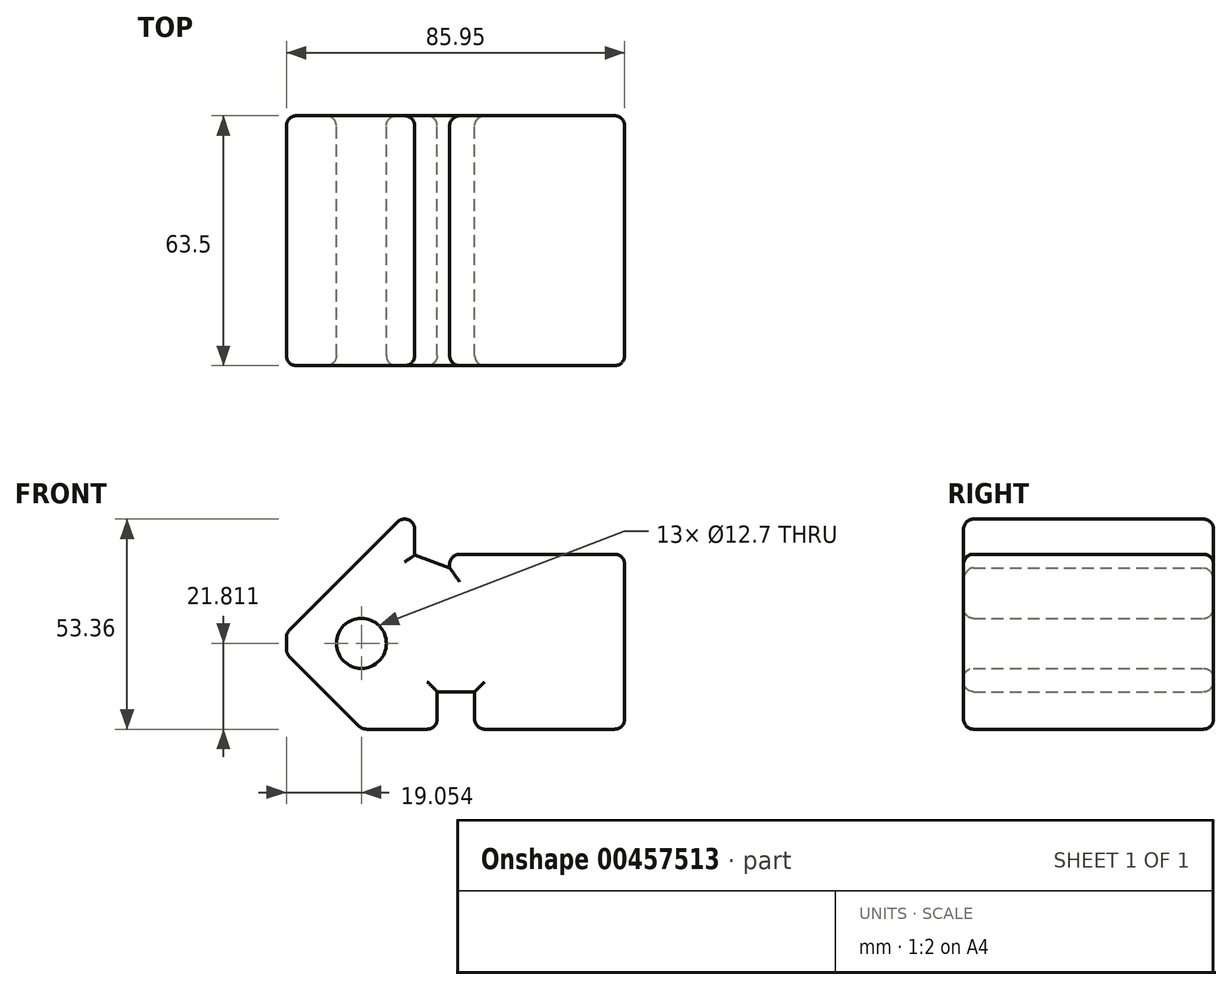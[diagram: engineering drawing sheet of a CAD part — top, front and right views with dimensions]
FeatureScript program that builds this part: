
annotation { "Feature Type Name" : "Feature", "Feature Type Description" : "" }
export const myFeature = defineFeature(function(context is Context, id is Id, definition is map)
    precondition{}
    {
        {
            var Q0;
            Q0=qCreatedBy(makeId("Front.planeOp"),FACE);
            var sketch = newSketch(context, id + "F0", { "sketchPlane" : qUnion([Q0])});
            skLineSegment(sketch, "E0", {"start": v(-44.45, 0) * mm, "end": v(0, 0) * mm});
            skLineSegment(sketch, "E1", {"start": v(0, 0) * mm, "end": v(0, -44.45) * mm});
            skLineSegment(sketch, "E2", {"start": v(0, -44.45) * mm, "end": v(-38.1, -44.45) * mm});
            skLineSegment(sketch, "E3", {"start": v(-38.1, -44.45) * mm, "end": v(-38.1, -34.93) * mm});
            skLineSegment(sketch, "E4", {"start": v(-38.1, -34.93) * mm, "end": v(-47.62, -34.93) * mm});
            skLineSegment(sketch, "E5", {"start": v(-47.62, -34.93) * mm, "end": v(-47.62, -44.45) * mm});
            skLineSegment(sketch, "E6", {"start": v(-47.62, -44.45) * mm, "end": v(-66.67, -44.45) * mm});
            skLineSegment(sketch, "E7", {"start": v(-66.68, -44.45) * mm, "end": v(-85.95, -25.18) * mm});
            skLineSegment(sketch, "E8", {"start": v(-85.95, -25.18) * mm, "end": v(-85.95, -20.1) * mm});
            skLineSegment(sketch, "E9", {"start": v(-85.95, -20.1) * mm, "end": v(-53.34, 12.5) * mm});
            skLineSegment(sketch, "E10", {"start": v(-53.34, 12.5) * mm, "end": v(-53.34, -0.2) * mm});
            skLineSegment(sketch, "E11", {"start": v(-53.34, -0.2) * mm, "end": v(-44.45, -3.43) * mm});
            skLineSegment(sketch, "E12", {"start": v(-44.45, -3.43) * mm, "end": v(-44.45, 0) * mm});
            skSolve(sketch);
        }
        {
            var Q0;
            Q0 = qSketchRegion(id + "F0", true);
            extrude(context, id + "F1", {"entities" : qUnion([Q0]), "depth" : 63.5 * mm});
        }
        {
            var Q0;
            Q0=qCreatedBy(makeId("Front.planeOp"),FACE);
            var sketch = newSketch(context, id + "F2", { "sketchPlane" : qUnion([Q0])});
            skCircle(sketch, "E13", {"center": v(-66.9, -22.64) * mm, "radius": 6.35 * mm});
            skLineSegment(sketch, "E14", {"start": v(-66.9, -22.64) * mm, "end": v(-85.95, -22.64) * mm, "construction": true});
            skSolve(sketch);
        }
        {
            var Q0;
            Q0 = qSketchRegion(id + "F2", true);
            extrude(context, id + "F3", {"entities" : qUnion([Q0]), "operationType" : NewBodyOperationType.REMOVE, "endBound" : BoundingType.THROUGH_ALL, "depth" : 25.4 * mm});
        }
        {
            var Q0;
            Q0=makeQuery(id+"F1.opExtrude","CAP_FACE",FACE,{"disambiguationData":[OSD([sQuery(id+"F0.wireOp",EDGE,"E0"),sQuery(id+"F0.wireOp",EDGE,"E1"),sQuery(id+"F0.wireOp",EDGE,"E2"),sQuery(id+"F0.wireOp",EDGE,"E3"),sQuery(id+"F0.wireOp",EDGE,"E4"),sQuery(id+"F0.wireOp",EDGE,"E5"),sQuery(id+"F0.wireOp",EDGE,"E6"),sQuery(id+"F0.wireOp",EDGE,"E7"),sQuery(id+"F0.wireOp",EDGE,"E8"),sQuery(id+"F0.wireOp",EDGE,"E9"),sQuery(id+"F0.wireOp",EDGE,"E10"),sQuery(id+"F0.wireOp",EDGE,"E11"),sQuery(id+"F0.wireOp",EDGE,"E12")])],"isStart":true});
            var Q1;
            Q1=makeQuery(id+"F1.opExtrude","SWEPT_FACE",FACE,{"disambiguationData":[OSD([sQuery(id+"F0.wireOp",EDGE,"E7")])]});
            var Q2;
            Q2=makeQuery(id+"F1.opExtrude","SWEPT_FACE",FACE,{"disambiguationData":[OSD([sQuery(id+"F0.wireOp",EDGE,"E2")])]});
            var Q3;
            Q3=makeQuery(id+"F1.opExtrude","CAP_FACE",FACE,{"disambiguationData":[OSD([sQuery(id+"F0.wireOp",EDGE,"E0"),sQuery(id+"F0.wireOp",EDGE,"E1"),sQuery(id+"F0.wireOp",EDGE,"E2"),sQuery(id+"F0.wireOp",EDGE,"E3"),sQuery(id+"F0.wireOp",EDGE,"E4"),sQuery(id+"F0.wireOp",EDGE,"E5"),sQuery(id+"F0.wireOp",EDGE,"E6"),sQuery(id+"F0.wireOp",EDGE,"E7"),sQuery(id+"F0.wireOp",EDGE,"E8"),sQuery(id+"F0.wireOp",EDGE,"E9"),sQuery(id+"F0.wireOp",EDGE,"E10"),sQuery(id+"F0.wireOp",EDGE,"E11"),sQuery(id+"F0.wireOp",EDGE,"E12")])],"isStart":false});
            var Q4;
            Q4=makeQuery(id+"F1.opExtrude","SWEPT_FACE",FACE,{"disambiguationData":[OSD([sQuery(id+"F0.wireOp",EDGE,"E6")])]});
            var Q5;
            Q5=makeQuery(id+"F1.opExtrude","SWEPT_FACE",FACE,{"disambiguationData":[OSD([sQuery(id+"F0.wireOp",EDGE,"E0")])]});
            var Q6;
            Q6=makeQuery(id+"F1.opExtrude","SWEPT_FACE",FACE,{"disambiguationData":[OSD([sQuery(id+"F0.wireOp",EDGE,"E9")])]});
            fillet(context, id + "F4", {"entities" : qUnion([Q0, Q1, Q2, Q3, Q4, Q5, Q6]), "radius" : 2.54 * mm, "tangentPropagation" : true, "allowEdgeOverflow" : false});
        }
    });
